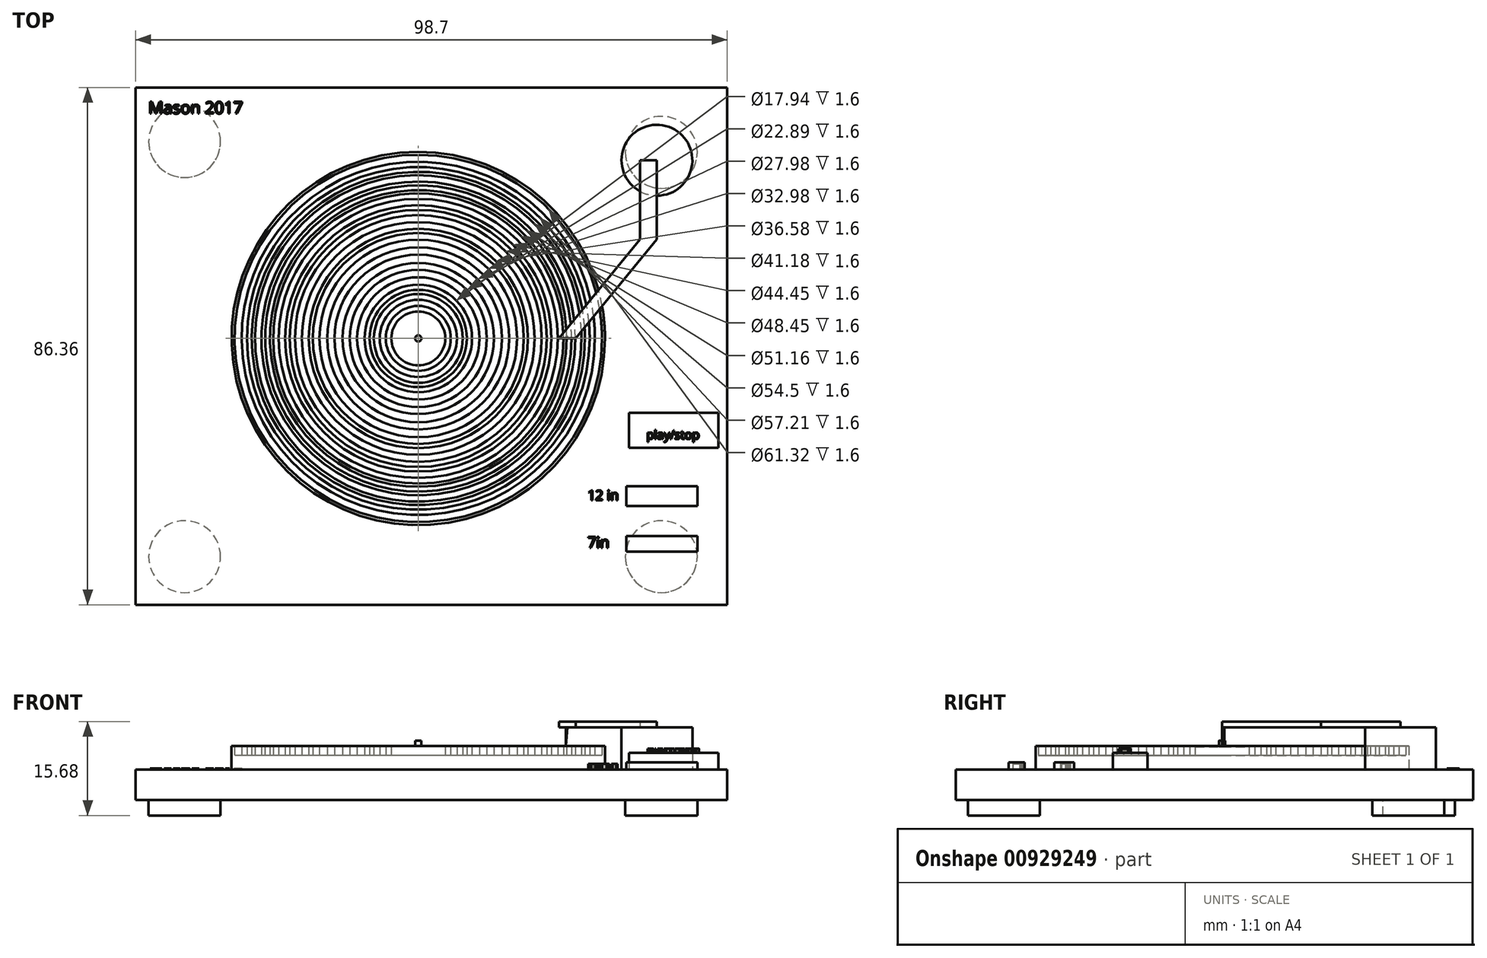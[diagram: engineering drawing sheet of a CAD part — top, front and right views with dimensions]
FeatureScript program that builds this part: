
annotation { "Feature Type Name" : "Feature", "Feature Type Description" : "" }
export const myFeature = defineFeature(function(context is Context, id is Id, definition is map)
    precondition{}
    {
        {
            var Q0;
            Q0=qCreatedBy(makeId("Top.planeOp"),FACE);
            var sketch = newSketch(context, id + "F0", { "sketchPlane" : qUnion([Q0])});
            skLineSegment(sketch, "E0.bottom", {"start": v(-47.16, 41.9) * mm, "end": v(51.54, 41.9) * mm});
            skLineSegment(sketch, "E0.top", {"start": v(-47.16, -44.46) * mm, "end": v(51.54, -44.46) * mm});
            skLineSegment(sketch, "E0.left", {"start": v(-47.16, 41.9) * mm, "end": v(-47.16, -44.46) * mm});
            skLineSegment(sketch, "E0.right", {"start": v(51.54, 41.9) * mm, "end": v(51.54, -44.46) * mm});
            skSolve(sketch);
        }
        {
            var Q0;
            Q0 = qSketchRegion(id + "F0", true);
            extrude(context, id + "F1", {"entities" : qUnion([Q0]), "depth" : 5.08 * mm, "offsetDistance" : 25.4 * mm});
        }
        {
            var Q0;
            Q0=makeQuery(id+"F1.opExtrude","CAP_FACE",FACE,{"disambiguationData":[OSD([sQuery(id+"F0.wireOp",EDGE,"E0.bottom"),sQuery(id+"F0.wireOp",EDGE,"E0.top"),sQuery(id+"F0.wireOp",EDGE,"E0.left"),sQuery(id+"F0.wireOp",EDGE,"E0.right")])],"isStart":false});
            var sketch = newSketch(context, id + "F2", { "sketchPlane" : qUnion([Q0])});
            skCircle(sketch, "E1", {"center": v(0, 0) * mm, "radius": 31.16 * mm});
            skSolve(sketch);
        }
        {
            var Q0;
            Q0 = qSketchRegion(id + "F2", true);
            extrude(context, id + "F3", {"entities" : qUnion([Q0]), "operationType" : NewBodyOperationType.ADD, "depth" : 2.3 * mm, "offsetDistance" : 25 * mm});
        }
        {
            var Q0;
            Q0=makeQuery(id+"F3.opExtrude","CAP_FACE",FACE,{"disambiguationData":[OSD([sQuery(id+"F2.wireOp",EDGE,"E1")])],"isStart":false});
            var sketch = newSketch(context, id + "F4", { "sketchPlane" : qUnion([Q0])});
            skCircle(sketch, "E2", {"center": v(0, 0) * mm, "radius": 5.42 * mm});
            skCircle(sketch, "E3", {"center": v(0, 0) * mm, "radius": 6.45 * mm});
            skCircle(sketch, "E4", {"center": v(0, 0) * mm, "radius": 7.42 * mm});
            skCircle(sketch, "E5", {"center": v(0, 0) * mm, "radius": 8.12 * mm});
            skCircle(sketch, "E6", {"center": v(0, 0) * mm, "radius": 8.97 * mm});
            skCircle(sketch, "E7", {"center": v(0, 0) * mm, "radius": 10.21 * mm});
            skCircle(sketch, "E8", {"center": v(0, 0) * mm, "radius": 11.44 * mm});
            skCircle(sketch, "E9", {"center": v(0, 0) * mm, "radius": 12.63 * mm});
            skCircle(sketch, "E10", {"center": v(0, 0) * mm, "radius": 14 * mm});
            skCircle(sketch, "E11", {"center": v(0, 0) * mm, "radius": 15.19 * mm});
            skCircle(sketch, "E12", {"center": v(0, 0) * mm, "radius": 16.49 * mm});
            skCircle(sketch, "E13", {"center": v(0, 0) * mm, "radius": 18.3 * mm});
            skCircle(sketch, "E14", {"center": v(0, 0) * mm, "radius": 19.42 * mm});
            skCircle(sketch, "E15", {"center": v(0, 0) * mm, "radius": 17.6 * mm});
            skCircle(sketch, "E16", {"center": v(0, 0) * mm, "radius": 20.59 * mm});
            skCircle(sketch, "E17", {"center": v(0, 0) * mm, "radius": 21.45 * mm});
            skCircle(sketch, "E18", {"center": v(0, 0) * mm, "radius": 23.3 * mm});
            skCircle(sketch, "E19", {"center": v(0, 0) * mm, "radius": 24.76 * mm});
            skCircle(sketch, "E20", {"center": v(0, 0) * mm, "radius": 22.23 * mm});
            skCircle(sketch, "E21", {"center": v(0, 0) * mm, "radius": 24.23 * mm});
            skCircle(sketch, "E22", {"center": v(0, 0) * mm, "radius": 26.2 * mm});
            skCircle(sketch, "E23", {"center": v(0, 0) * mm, "radius": 25.58 * mm});
            skCircle(sketch, "E24", {"center": v(0, 0) * mm, "radius": 27.81 * mm});
            skCircle(sketch, "E25", {"center": v(0, 0) * mm, "radius": 27.25 * mm});
            skCircle(sketch, "E26", {"center": v(0, 0) * mm, "radius": 29.49 * mm});
            skCircle(sketch, "E27", {"center": v(0, 0) * mm, "radius": 30.66 * mm});
            skCircle(sketch, "E28", {"center": v(0, 0) * mm, "radius": 28.6 * mm});
            skSolve(sketch);
        }
        {
            var Q0;
            Q0=makeQuery(id+"F4.imprint","IMPRINT",FACE,{"disambiguationData":[TD([[makeQuery(id+"F4.imprint","IMPRINT",EDGE,{"derivedFrom":sQuery(id+"F4.wireOp",EDGE,"E2")}),-1.0]])]});
            var Q1;
            Q1=makeQuery(id+"F4.imprint","IMPRINT",FACE,{"disambiguationData":[TD([[makeQuery(id+"F4.imprint","IMPRINT",EDGE,{"derivedFrom":sQuery(id+"F4.wireOp",EDGE,"E4")}),-1.0]])]});
            var Q2;
            Q2=makeQuery(id+"F4.imprint","IMPRINT",FACE,{"disambiguationData":[TD([[makeQuery(id+"F4.imprint","IMPRINT",EDGE,{"derivedFrom":sQuery(id+"F4.wireOp",EDGE,"E6")}),-1.0]])]});
            var Q3;
            Q3=makeQuery(id+"F4.imprint","IMPRINT",FACE,{"disambiguationData":[TD([[makeQuery(id+"F4.imprint","IMPRINT",EDGE,{"derivedFrom":sQuery(id+"F4.wireOp",EDGE,"E8")}),-1.0]])]});
            var Q4;
            Q4=makeQuery(id+"F4.imprint","IMPRINT",FACE,{"disambiguationData":[TD([[makeQuery(id+"F4.imprint","IMPRINT",EDGE,{"derivedFrom":sQuery(id+"F4.wireOp",EDGE,"E10")}),-1.0]])]});
            var Q5;
            Q5=makeQuery(id+"F4.imprint","IMPRINT",FACE,{"disambiguationData":[TD([[makeQuery(id+"F4.imprint","IMPRINT",EDGE,{"derivedFrom":sQuery(id+"F4.wireOp",EDGE,"E12")}),-1.0]])]});
            var Q6;
            Q6=makeQuery(id+"F4.imprint","IMPRINT",FACE,{"disambiguationData":[TD([[makeQuery(id+"F4.imprint","IMPRINT",EDGE,{"derivedFrom":sQuery(id+"F4.wireOp",EDGE,"E13")}),-1.0]])]});
            var Q7;
            Q7=makeQuery(id+"F4.imprint","IMPRINT",FACE,{"disambiguationData":[TD([[makeQuery(id+"F4.imprint","IMPRINT",EDGE,{"derivedFrom":sQuery(id+"F4.wireOp",EDGE,"E16")}),-1.0]])]});
            var Q8;
            Q8=makeQuery(id+"F4.imprint","IMPRINT",FACE,{"disambiguationData":[TD([[makeQuery(id+"F4.imprint","IMPRINT",EDGE,{"derivedFrom":sQuery(id+"F4.wireOp",EDGE,"E18")}),1.0]])]});
            var Q9;
            Q9=makeQuery(id+"F4.imprint","IMPRINT",FACE,{"disambiguationData":[TD([[makeQuery(id+"F4.imprint","IMPRINT",EDGE,{"derivedFrom":sQuery(id+"F4.wireOp",EDGE,"E19")}),1.0]])]});
            var Q10;
            Q10=makeQuery(id+"F4.imprint","IMPRINT",FACE,{"disambiguationData":[TD([[makeQuery(id+"F4.imprint","IMPRINT",EDGE,{"derivedFrom":sQuery(id+"F4.wireOp",EDGE,"E22")}),1.0]])]});
            var Q11;
            Q11=makeQuery(id+"F4.imprint","IMPRINT",FACE,{"disambiguationData":[TD([[makeQuery(id+"F4.imprint","IMPRINT",EDGE,{"derivedFrom":sQuery(id+"F4.wireOp",EDGE,"E24")}),1.0]])]});
            var Q12;
            Q12=makeQuery(id+"F4.imprint","IMPRINT",FACE,{"disambiguationData":[TD([[makeQuery(id+"F4.imprint","IMPRINT",EDGE,{"derivedFrom":sQuery(id+"F4.wireOp",EDGE,"E26")}),1.0]])]});
            var Q13;
            Q13=makeQuery(id+"F4.imprint","IMPRINT",FACE,{"disambiguationData":[TD([[makeQuery(id+"F4.imprint","IMPRINT",EDGE,{"derivedFrom":sQuery(id+"F4.wireOp",EDGE,"E27")}),-1.0]])]});
            extrude(context, id + "F5", {"entities" : qUnion([Q0, Q1, Q2, Q3, Q4, Q5, Q6, Q7, Q8, Q9, Q10, Q11, Q12, Q13]), "operationType" : NewBodyOperationType.ADD, "depth" : 1.6 * mm, "offsetDistance" : 25 * mm});
        }
        {
            var Q0;
            Q0=makeQuery(id+"F1.opExtrude","CAP_FACE",FACE,{"disambiguationData":[OSD([sQuery(id+"F0.wireOp",EDGE,"E0.bottom"),sQuery(id+"F0.wireOp",EDGE,"E0.top"),sQuery(id+"F0.wireOp",EDGE,"E0.left"),sQuery(id+"F0.wireOp",EDGE,"E0.right")])],"isStart":false});
            var sketch = newSketch(context, id + "F6", { "sketchPlane" : qUnion([Q0])});
            skCircle(sketch, "E29", {"center": v(39.84, 29.75) * mm, "radius": 5.91 * mm});
            skSolve(sketch);
        }
        {
            var Q0;
            Q0 = qSketchRegion(id + "F6", true);
            extrude(context, id + "F7", {"entities" : qUnion([Q0]), "operationType" : NewBodyOperationType.ADD, "depth" : 7 * mm, "offsetDistance" : 25 * mm});
        }
        {
            var Q0;
            Q0=makeQuery(id+"F7.opExtrude","CAP_FACE",FACE,{"disambiguationData":[OSD([sQuery(id+"F6.wireOp",EDGE,"E29")])],"isStart":false});
            var sketch = newSketch(context, id + "F8", { "sketchPlane" : qUnion([Q0])});
            skLineSegment(sketch, "E30", {"start": v(39.84, 29.75) * mm, "end": v(39.84, 16.51) * mm});
            skLineSegment(sketch, "E31", {"start": v(39.84, 16.51) * mm, "end": v(26.27, 0) * mm});
            skLineSegment(sketch, "E32", {"start": v(37.04, 29.75) * mm, "end": v(37.04, 16.51) * mm});
            skLineSegment(sketch, "E33", {"start": v(37.04, 16.51) * mm, "end": v(23.47, 0) * mm});
            skLineSegment(sketch, "E34", {"start": v(23.47, 0) * mm, "end": v(26.27, 0) * mm});
            skLineSegment(sketch, "E35", {"start": v(37.04, 29.75) * mm, "end": v(39.84, 29.75) * mm});
            skSolve(sketch);
        }
        {
            var Q0;
            {var subQ4=sQuery(id+"F8.wireOp",EDGE,"E31");Q0=makeQuery(id+"F8.imprint","IMPRINT",FACE,{"disambiguationData":[TD([[makeQuery(id+"F8.imprint","IMPRINT",EDGE,{"derivedFrom":subQ4}),-1.0]])]});}
            var Q1;
            {var subQ0=sQuery(id+"F8.wireOp",EDGE,"E35");Q1=makeQuery(id+"F8.imprint","IMPRINT",FACE,{"disambiguationData":[TD([[makeQuery(id+"F8.imprint","IMPRINT",EDGE,{"derivedFrom":subQ0}),-1.0]])]});}
            extrude(context, id + "F9", {"entities" : qUnion([Q0, Q1]), "operationType" : NewBodyOperationType.ADD, "depth" : 1 * mm, "offsetDistance" : 25 * mm});
        }
        {
            var Q0;
            Q0=makeQuery(id+"F9.opExtrude","SWEPT_FACE",FACE,{"disambiguationData":[OSD([sQuery(id+"F8.wireOp",EDGE,"E34")])]});
            var sketch = newSketch(context, id + "F10", { "sketchPlane" : qUnion([Q0])});
            skLineSegment(sketch, "E36", {"start": v(24.87, 12.08) * mm, "end": v(24.65, 8.95) * mm});
            skLineSegment(sketch, "E37", {"start": v(24.65, 8.95) * mm, "end": v(24.65, 12.08) * mm});
            skSolve(sketch);
        }
        {
            var Q0;
            {var subQ0=sQuery(id+"F10.wireOp",EDGE,"E36");Q0=makeQuery(id+"F10.imprint","IMPRINT",FACE,{"disambiguationData":[TD([[makeQuery(id+"F10.imprint","IMPRINT",EDGE,{"derivedFrom":subQ0}),-1.0]])]});}
            extrude(context, id + "F11", {"entities" : qUnion([Q0]), "oppositeDirection" : true, "depth" : 0.4 * mm, "offsetDistance" : 25 * mm});
        }
        {
            var Q0;
            Q0=makeQuery(id+"F5.boolean.opBoolean","SPLIT",FACE,{"disambiguationData":[TD([makeQuery(id+"F5.opExtrude","SWEPT_FACE",FACE,{"disambiguationData":[OSD([sQuery(id+"F4.wireOp",EDGE,"E2")])]})])],"derivedFrom":makeQuery(id+"F3.opExtrude","CAP_FACE",FACE,{"disambiguationData":[OSD([sQuery(id+"F2.wireOp",EDGE,"E1")])],"isStart":false})});
            var sketch = newSketch(context, id + "F12", { "sketchPlane" : qUnion([Q0])});
            skCircle(sketch, "E38", {"center": v(0, 0) * mm, "radius": 4.5 * mm});
            skSolve(sketch);
        }
        {
            var Q0;
            Q0=makeQuery(id+"F12.imprint","IMPRINT",FACE,{"disambiguationData":[TD([[makeQuery(id+"F12.imprint","IMPRINT",EDGE,{"derivedFrom":sQuery(id+"F12.wireOp",EDGE,"E38")}),1.0]])]});
            extrude(context, id + "F13", {"entities" : qUnion([Q0]), "operationType" : NewBodyOperationType.ADD, "depth" : 1.5 * mm, "offsetDistance" : 25 * mm});
        }
        {
            var Q0;
            Q0=makeQuery(id+"F13.opExtrude","CAP_FACE",FACE,{"disambiguationData":[OSD([sQuery(id+"F12.wireOp",EDGE,"E38")])],"isStart":false});
            var sketch = newSketch(context, id + "F14", { "sketchPlane" : qUnion([Q0])});
            skCircle(sketch, "E39", {"center": v(0, 0) * mm, "radius": 0.52 * mm});
            skSolve(sketch);
        }
        {
            var Q0;
            Q0=makeQuery(id+"F14.imprint","IMPRINT",FACE,{"disambiguationData":[TD([[makeQuery(id+"F14.imprint","IMPRINT",EDGE,{"derivedFrom":sQuery(id+"F14.wireOp",EDGE,"E39")}),1.0]])]});
            extrude(context, id + "F15", {"entities" : qUnion([Q0]), "operationType" : NewBodyOperationType.ADD, "depth" : 1 * mm, "offsetDistance" : 25 * mm});
        }
        {
            var Q0;
            Q0=makeQuery(id+"F1.opExtrude","CAP_FACE",FACE,{"disambiguationData":[OSD([sQuery(id+"F0.wireOp",EDGE,"E0.bottom"),sQuery(id+"F0.wireOp",EDGE,"E0.top"),sQuery(id+"F0.wireOp",EDGE,"E0.left"),sQuery(id+"F0.wireOp",EDGE,"E0.right")])],"isStart":true});
            var sketch = newSketch(context, id + "F16", { "sketchPlane" : qUnion([Q0])});
            skCircle(sketch, "E40", {"center": v(-39, 36.43) * mm, "radius": 6 * mm});
            skCircle(sketch, "E41", {"center": v(40.57, 36.43) * mm, "radius": 6 * mm});
            skCircle(sketch, "E42", {"center": v(40.57, -31.07) * mm, "radius": 6 * mm});
            skCircle(sketch, "E43", {"center": v(-39, -32.87) * mm, "radius": 6 * mm});
            skSolve(sketch);
        }
        {
            var Q0;
            Q0=makeQuery(id+"F16.imprint","IMPRINT",FACE,{"disambiguationData":[TD([[makeQuery(id+"F16.imprint","IMPRINT",EDGE,{"derivedFrom":sQuery(id+"F16.wireOp",EDGE,"E40")}),1.0]])]});
            var Q1;
            Q1=makeQuery(id+"F16.imprint","IMPRINT",FACE,{"disambiguationData":[TD([[makeQuery(id+"F16.imprint","IMPRINT",EDGE,{"derivedFrom":sQuery(id+"F16.wireOp",EDGE,"E41")}),1.0]])]});
            var Q2;
            Q2=makeQuery(id+"F16.imprint","IMPRINT",FACE,{"disambiguationData":[TD([[makeQuery(id+"F16.imprint","IMPRINT",EDGE,{"derivedFrom":sQuery(id+"F16.wireOp",EDGE,"E42")}),1.0]])]});
            var Q3;
            Q3=makeQuery(id+"F16.imprint","IMPRINT",FACE,{"disambiguationData":[TD([[makeQuery(id+"F16.imprint","IMPRINT",EDGE,{"derivedFrom":sQuery(id+"F16.wireOp",EDGE,"E43")}),1.0]])]});
            extrude(context, id + "F17", {"entities" : qUnion([Q0, Q1, Q2, Q3]), "operationType" : NewBodyOperationType.ADD, "depth" : 2.6 * mm, "offsetDistance" : 25 * mm});
        }
        {
            var Q0;
            Q0=makeQuery(id+"F1.opExtrude","CAP_FACE",FACE,{"disambiguationData":[OSD([sQuery(id+"F0.wireOp",EDGE,"E0.bottom"),sQuery(id+"F0.wireOp",EDGE,"E0.top"),sQuery(id+"F0.wireOp",EDGE,"E0.left"),sQuery(id+"F0.wireOp",EDGE,"E0.right")])],"isStart":false});
            var sketch = newSketch(context, id + "F18", { "sketchPlane" : qUnion([Q0])});
            skLineSegment(sketch, "E44.bottom", {"start": v(34.7, -24.7) * mm, "end": v(46.62, -24.7) * mm});
            skLineSegment(sketch, "E44.top", {"start": v(34.7, -28) * mm, "end": v(46.62, -28) * mm});
            skLineSegment(sketch, "E44.left", {"start": v(34.7, -24.7) * mm, "end": v(34.7, -28) * mm});
            skLineSegment(sketch, "E44.right", {"start": v(46.62, -24.7) * mm, "end": v(46.62, -28) * mm});
            skLineSegment(sketch, "E45.bottom", {"start": v(34.7, -32.97) * mm, "end": v(46.62, -32.97) * mm});
            skLineSegment(sketch, "E45.top", {"start": v(34.7, -35.61) * mm, "end": v(46.62, -35.61) * mm});
            skLineSegment(sketch, "E45.left", {"start": v(34.7, -32.97) * mm, "end": v(34.7, -35.61) * mm});
            skLineSegment(sketch, "E45.right", {"start": v(46.62, -32.97) * mm, "end": v(46.62, -35.61) * mm});
            skSolve(sketch);
        }
        {
            var Q0;
            Q0 = qSketchRegion(id + "F18", true);
            extrude(context, id + "F19", {"entities" : qUnion([Q0]), "operationType" : NewBodyOperationType.ADD, "depth" : 1.2 * mm, "offsetDistance" : 25 * mm});
        }
        {
            var Q0;
            Q0=makeQuery(id+"F1.opExtrude","CAP_FACE",FACE,{"disambiguationData":[OSD([sQuery(id+"F0.wireOp",EDGE,"E0.bottom"),sQuery(id+"F0.wireOp",EDGE,"E0.top"),sQuery(id+"F0.wireOp",EDGE,"E0.left"),sQuery(id+"F0.wireOp",EDGE,"E0.right")])],"isStart":false});
            var sketch = newSketch(context, id + "F20", { "sketchPlane" : qUnion([Q0])});
            skText(sketch, "E46", { "text": "12 in", "fontName": "OpenSans-Regular.ttf"});
            skText(sketch, "E47", { "text": "7in", "fontName": "OpenSans-Regular.ttf"});
            const initialGuessF20  = {"E46": [0.02825, -0.027, 1, 0, 0.00165], "E47": [0.02825, -0.03495, 1, 0, 0.00182]};
            skSetInitialGuess(sketch, initialGuessF20);
            skSolve(sketch);
        }
        {
            var Q0;
            Q0=makeQuery(id+"F20.imprint","IMPRINT",FACE,{"disambiguationData":[TD([[makeQuery(id+"F20.imprint","IMPRINT",EDGE,{"derivedFrom":sQuery(id+"F20.wireOp",EDGE,"E47.sketch_text.stroke-0")}),-1.0]])]});
            var Q1;
            Q1=makeQuery(id+"F20.imprint","IMPRINT",FACE,{"disambiguationData":[TD([[makeQuery(id+"F20.imprint","IMPRINT",EDGE,{"derivedFrom":sQuery(id+"F20.wireOp",EDGE,"E47.sketch_text.stroke-7")}),-1.0]])]});
            var Q2;
            Q2=makeQuery(id+"F20.imprint","IMPRINT",FACE,{"disambiguationData":[TD([[makeQuery(id+"F20.imprint","IMPRINT",EDGE,{"derivedFrom":sQuery(id+"F20.wireOp",EDGE,"E47.sketch_text.stroke-11")}),-1.0]])]});
            var Q3;
            Q3=makeQuery(id+"F20.imprint","IMPRINT",FACE,{"disambiguationData":[TD([[makeQuery(id+"F20.imprint","IMPRINT",EDGE,{"derivedFrom":sQuery(id+"F20.wireOp",EDGE,"E47.sketch_text.stroke-19")}),-1.0]])]});
            var Q4;
            Q4=makeQuery(id+"F20.imprint","IMPRINT",FACE,{"disambiguationData":[TD([[makeQuery(id+"F20.imprint","IMPRINT",EDGE,{"derivedFrom":sQuery(id+"F20.wireOp",EDGE,"E46.sketch_text.stroke-9")}),-1.0]])]});
            var Q5;
            Q5=makeQuery(id+"F20.imprint","IMPRINT",FACE,{"disambiguationData":[TD([[makeQuery(id+"F20.imprint","IMPRINT",EDGE,{"derivedFrom":sQuery(id+"F20.wireOp",EDGE,"E46.sketch_text.stroke-0")}),-1.0]])]});
            var Q6;
            Q6=makeQuery(id+"F20.imprint","IMPRINT",FACE,{"disambiguationData":[TD([[makeQuery(id+"F20.imprint","IMPRINT",EDGE,{"derivedFrom":sQuery(id+"F20.wireOp",EDGE,"E46.sketch_text.stroke-29")}),-1.0]])]});
            var Q7;
            Q7=makeQuery(id+"F20.imprint","IMPRINT",FACE,{"disambiguationData":[TD([[makeQuery(id+"F20.imprint","IMPRINT",EDGE,{"derivedFrom":sQuery(id+"F20.wireOp",EDGE,"E46.sketch_text.stroke-33")}),-1.0]])]});
            var Q8;
            Q8=makeQuery(id+"F20.imprint","IMPRINT",FACE,{"disambiguationData":[TD([[makeQuery(id+"F20.imprint","IMPRINT",EDGE,{"derivedFrom":sQuery(id+"F20.wireOp",EDGE,"E46.sketch_text.stroke-41")}),-1.0]])]});
            extrude(context, id + "F21", {"entities" : qUnion([Q0, Q1, Q2, Q3, Q4, Q5, Q6, Q7, Q8]), "operationType" : NewBodyOperationType.ADD, "depth" : 0.9 * mm, "offsetDistance" : 25 * mm});
        }
        {
            var Q0;
            Q0=makeQuery(id+"F1.opExtrude","CAP_FACE",FACE,{"disambiguationData":[OSD([sQuery(id+"F0.wireOp",EDGE,"E0.bottom"),sQuery(id+"F0.wireOp",EDGE,"E0.top"),sQuery(id+"F0.wireOp",EDGE,"E0.left"),sQuery(id+"F0.wireOp",EDGE,"E0.right")])],"isStart":false});
            var sketch = newSketch(context, id + "F22", { "sketchPlane" : qUnion([Q0])});
            skLineSegment(sketch, "E48.bottom", {"start": v(35.2, -12.45) * mm, "end": v(50.1, -12.45) * mm});
            skLineSegment(sketch, "E48.top", {"start": v(35.2, -18.24) * mm, "end": v(50.1, -18.24) * mm});
            skLineSegment(sketch, "E48.left", {"start": v(35.2, -12.45) * mm, "end": v(35.2, -18.24) * mm});
            skLineSegment(sketch, "E48.right", {"start": v(50.1, -12.45) * mm, "end": v(50.1, -18.24) * mm});
            skSolve(sketch);
        }
        {
            var Q0;
            Q0=makeQuery(id+"F22.imprint","IMPRINT",FACE,{"disambiguationData":[TD([[makeQuery(id+"F22.imprint","IMPRINT",EDGE,{"derivedFrom":sQuery(id+"F22.wireOp",EDGE,"E48.bottom")}),-1.0]])]});
            extrude(context, id + "F23", {"entities" : qUnion([Q0]), "operationType" : NewBodyOperationType.ADD, "depth" : 2.8 * mm, "offsetDistance" : 25 * mm});
        }
        {
            var Q0;
            Q0=makeQuery(id+"F23.opExtrude","CAP_FACE",FACE,{"disambiguationData":[OSD([sQuery(id+"F22.wireOp",EDGE,"E48.bottom"),sQuery(id+"F22.wireOp",EDGE,"E48.top"),sQuery(id+"F22.wireOp",EDGE,"E48.left"),sQuery(id+"F22.wireOp",EDGE,"E48.right")])],"isStart":false});
            var sketch = newSketch(context, id + "F24", { "sketchPlane" : qUnion([Q0])});
            skText(sketch, "E49", { "text": "play/stop", "fontName": "OpenSans-Regular.ttf"});
            skPoint(sketch, "E49.firstSnap0", {"position": v(35.2, -15.34) * mm});
            const initialGuessF24  = {"E49": [0.03808, -0.01681, 1, 0, 0.00147]};
            skSetInitialGuess(sketch, initialGuessF24);
            skSolve(sketch);
        }
        {
            var Q0;
            Q0=makeQuery(id+"F24.imprint","IMPRINT",FACE,{"disambiguationData":[TD([[makeQuery(id+"F24.imprint","IMPRINT",EDGE,{"derivedFrom":sQuery(id+"F24.wireOp",EDGE,"E49.sketch_text.stroke-0")}),-1.0]])]});
            var Q1;
            Q1=makeQuery(id+"F24.imprint","IMPRINT",FACE,{"disambiguationData":[TD([[makeQuery(id+"F24.imprint","IMPRINT",EDGE,{"derivedFrom":sQuery(id+"F24.wireOp",EDGE,"E49.sketch_text.stroke-25")}),-1.0]])]});
            var Q2;
            Q2=makeQuery(id+"F24.imprint","IMPRINT",FACE,{"disambiguationData":[TD([[makeQuery(id+"F24.imprint","IMPRINT",EDGE,{"derivedFrom":sQuery(id+"F24.wireOp",EDGE,"E49.sketch_text.stroke-29")}),-1.0]])]});
            var Q3;
            Q3=makeQuery(id+"F24.imprint","IMPRINT",FACE,{"disambiguationData":[TD([[makeQuery(id+"F24.imprint","IMPRINT",EDGE,{"derivedFrom":sQuery(id+"F24.wireOp",EDGE,"E49.sketch_text.stroke-56")}),-1.0]])]});
            var Q4;
            Q4=makeQuery(id+"F24.imprint","IMPRINT",FACE,{"disambiguationData":[TD([[makeQuery(id+"F24.imprint","IMPRINT",EDGE,{"derivedFrom":sQuery(id+"F24.wireOp",EDGE,"E49.sketch_text.stroke-72")}),-1.0]])]});
            var Q5;
            Q5=makeQuery(id+"F24.imprint","IMPRINT",FACE,{"disambiguationData":[TD([[makeQuery(id+"F24.imprint","IMPRINT",EDGE,{"derivedFrom":sQuery(id+"F24.wireOp",EDGE,"E49.sketch_text.stroke-76")}),-1.0]])]});
            var Q6;
            Q6=makeQuery(id+"F24.imprint","IMPRINT",FACE,{"disambiguationData":[TD([[makeQuery(id+"F24.imprint","IMPRINT",EDGE,{"derivedFrom":sQuery(id+"F24.wireOp",EDGE,"E49.sketch_text.stroke-101")}),-1.0]])]});
            var Q7;
            Q7=makeQuery(id+"F24.imprint","IMPRINT",FACE,{"disambiguationData":[TD([[makeQuery(id+"F24.imprint","IMPRINT",EDGE,{"derivedFrom":sQuery(id+"F24.wireOp",EDGE,"E49.sketch_text.stroke-120")}),-1.0]])]});
            var Q8;
            Q8=makeQuery(id+"F24.imprint","IMPRINT",FACE,{"disambiguationData":[TD([[makeQuery(id+"F24.imprint","IMPRINT",EDGE,{"derivedFrom":sQuery(id+"F24.wireOp",EDGE,"E49.sketch_text.stroke-137")}),-1.0]])]});
            extrude(context, id + "F25", {"entities" : qUnion([Q0, Q1, Q2, Q3, Q4, Q5, Q6, Q7, Q8]), "operationType" : NewBodyOperationType.ADD, "depth" : 0.7 * mm, "offsetDistance" : 25 * mm});
        }
        {
            var Q0;
            Q0=makeQuery(id+"F1.opExtrude","CAP_FACE",FACE,{"disambiguationData":[OSD([sQuery(id+"F0.wireOp",EDGE,"E0.bottom"),sQuery(id+"F0.wireOp",EDGE,"E0.top"),sQuery(id+"F0.wireOp",EDGE,"E0.left"),sQuery(id+"F0.wireOp",EDGE,"E0.right")])],"isStart":false});
            var sketch = newSketch(context, id + "F26", { "sketchPlane" : qUnion([Q0])});
            skText(sketch, "E50", { "text": "Mason 2017", "fontName": "OpenSans-Regular.ttf"});
            const initialGuessF26  = {"E50": [-0.04505, 0.03753, 1, 0, 0.00199]};
            skSetInitialGuess(sketch, initialGuessF26);
            skSolve(sketch);
        }
        {
            var Q0;
            Q0=makeQuery(id+"F26.imprint","IMPRINT",FACE,{"disambiguationData":[TD([[makeQuery(id+"F26.imprint","IMPRINT",EDGE,{"derivedFrom":sQuery(id+"F26.wireOp",EDGE,"E50.sketch_text.stroke-0")}),-1.0]])]});
            var Q1;
            Q1=makeQuery(id+"F26.imprint","IMPRINT",FACE,{"disambiguationData":[TD([[makeQuery(id+"F26.imprint","IMPRINT",EDGE,{"derivedFrom":sQuery(id+"F26.wireOp",EDGE,"E50.sketch_text.stroke-18")}),-1.0]])]});
            var Q2;
            Q2=makeQuery(id+"F26.imprint","IMPRINT",FACE,{"disambiguationData":[TD([[makeQuery(id+"F26.imprint","IMPRINT",EDGE,{"derivedFrom":sQuery(id+"F26.wireOp",EDGE,"E50.sketch_text.stroke-45")}),-1.0]])]});
            var Q3;
            Q3=makeQuery(id+"F26.imprint","IMPRINT",FACE,{"disambiguationData":[TD([[makeQuery(id+"F26.imprint","IMPRINT",EDGE,{"derivedFrom":sQuery(id+"F26.wireOp",EDGE,"E50.sketch_text.stroke-70")}),-1.0]])]});
            var Q4;
            Q4=makeQuery(id+"F26.imprint","IMPRINT",FACE,{"disambiguationData":[TD([[makeQuery(id+"F26.imprint","IMPRINT",EDGE,{"derivedFrom":sQuery(id+"F26.wireOp",EDGE,"E50.sketch_text.stroke-87")}),-1.0]])]});
            var Q5;
            Q5=makeQuery(id+"F26.imprint","IMPRINT",FACE,{"disambiguationData":[TD([[makeQuery(id+"F26.imprint","IMPRINT",EDGE,{"derivedFrom":sQuery(id+"F26.wireOp",EDGE,"E50.sketch_text.stroke-104")}),-1.0]])]});
            var Q6;
            Q6=makeQuery(id+"F26.imprint","IMPRINT",FACE,{"disambiguationData":[TD([[makeQuery(id+"F26.imprint","IMPRINT",EDGE,{"derivedFrom":sQuery(id+"F26.wireOp",EDGE,"E50.sketch_text.stroke-124")}),-1.0]])]});
            var Q7;
            Q7=makeQuery(id+"F26.imprint","IMPRINT",FACE,{"disambiguationData":[TD([[makeQuery(id+"F26.imprint","IMPRINT",EDGE,{"derivedFrom":sQuery(id+"F26.wireOp",EDGE,"E50.sketch_text.stroke-140")}),-1.0]])]});
            var Q8;
            Q8=makeQuery(id+"F26.imprint","IMPRINT",FACE,{"disambiguationData":[TD([[makeQuery(id+"F26.imprint","IMPRINT",EDGE,{"derivedFrom":sQuery(id+"F26.wireOp",EDGE,"E50.sketch_text.stroke-149")}),-1.0]])]});
            extrude(context, id + "F27", {"entities" : qUnion([Q0, Q1, Q2, Q3, Q4, Q5, Q6, Q7, Q8]), "operationType" : NewBodyOperationType.ADD, "depth" : 0.2 * mm, "offsetDistance" : 25 * mm});
        }
    });
